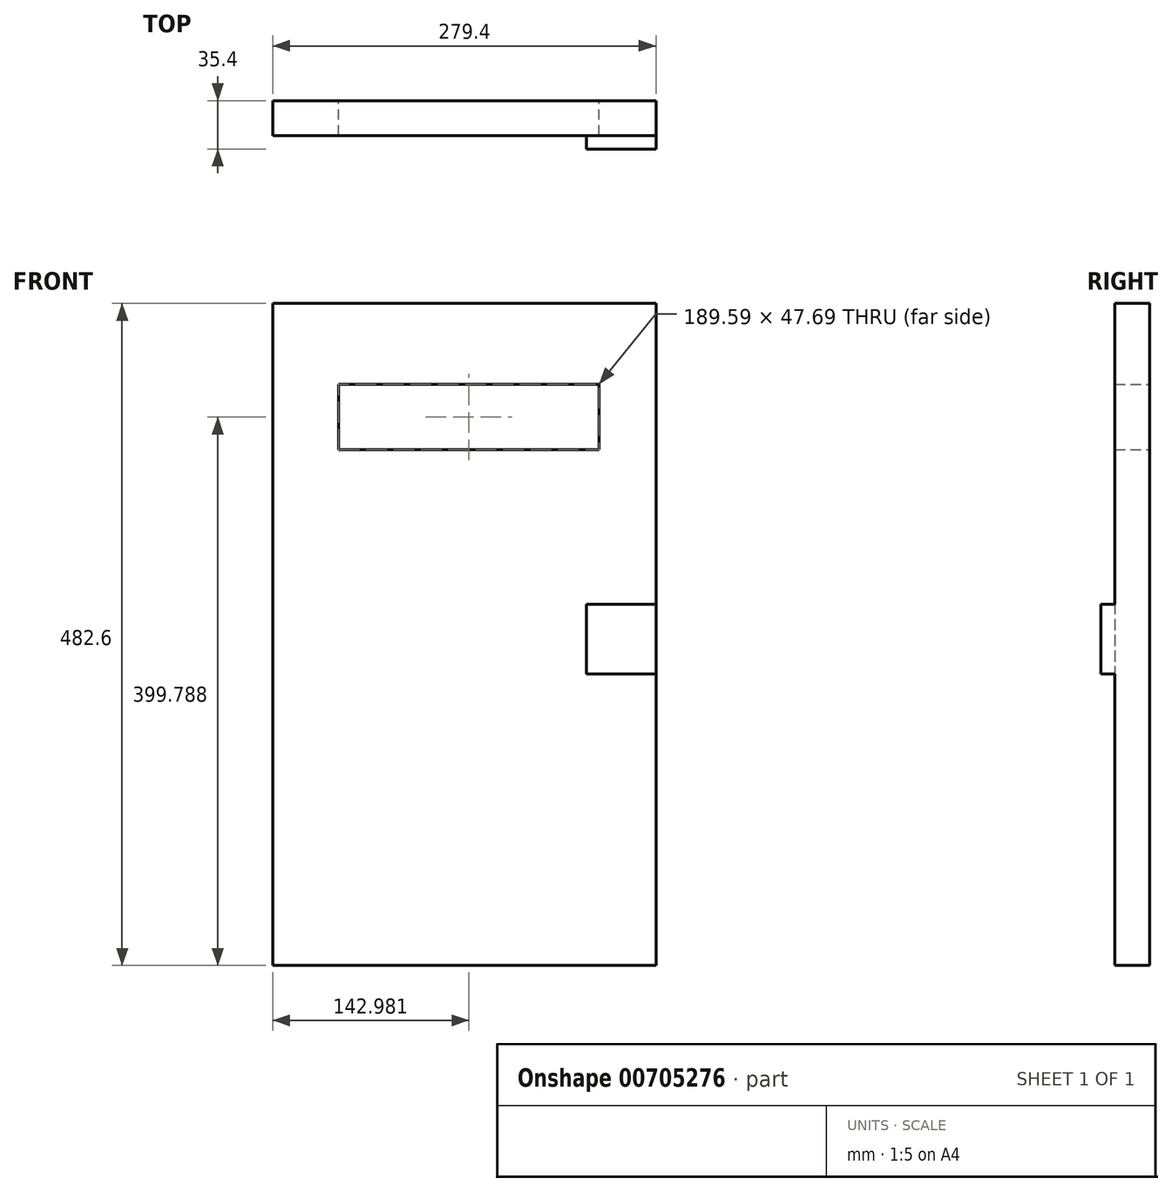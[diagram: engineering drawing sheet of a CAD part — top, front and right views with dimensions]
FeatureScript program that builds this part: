
annotation { "Feature Type Name" : "Feature", "Feature Type Description" : "" }
export const myFeature = defineFeature(function(context is Context, id is Id, definition is map)
    precondition{}
    {
        {
            var Q0;
            Q0=qCreatedBy(makeId("Front.planeOp"),FACE);
            var sketch = newSketch(context, id + "F0", { "sketchPlane" : qUnion([Q0])});
            skLineSegment(sketch, "E0.bottom", {"start": v(139.7, 241.3) * mm, "end": v(-139.7, 241.3) * mm});
            skLineSegment(sketch, "E0.top", {"start": v(139.7, -241.3) * mm, "end": v(-139.7, -241.3) * mm});
            skLineSegment(sketch, "E0.left", {"start": v(139.7, 241.3) * mm, "end": v(139.7, -241.3) * mm});
            skLineSegment(sketch, "E0.right", {"start": v(-139.7, 241.3) * mm, "end": v(-139.7, -241.3) * mm});
            skPoint(sketch, "E0.middle", {"position": v(0, 0) * mm});
            skLineSegment(sketch, "E1", {"start": v(-91.51, 182.33) * mm, "end": v(98.07, 182.33) * mm});
            skLineSegment(sketch, "E2", {"start": v(-91.51, 182.33) * mm, "end": v(-91.51, 134.64) * mm});
            skLineSegment(sketch, "E3", {"start": v(98.07, 182.33) * mm, "end": v(98.07, 134.64) * mm});
            skLineSegment(sketch, "E4", {"start": v(98.07, 134.64) * mm, "end": v(-91.51, 134.64) * mm});
            skLineSegment(sketch, "E5", {"start": v(-91.51, 158.49) * mm, "end": v(98.07, 158.49) * mm});
            skSolve(sketch);
        }
        {
            var Q0;
            Q0=makeQuery(id+"F0.imprint","IMPRINT",FACE,{"disambiguationData":[TD([[makeQuery(id+"F0.imprint","IMPRINT",EDGE,{"derivedFrom":sQuery(id+"F0.wireOp",EDGE,"E0.bottom")}),1.0]])]});
            extrude(context, id + "F1", {"entities" : qUnion([Q0]), "depth" : 25.4 * mm, "offsetDistance" : 25.4 * mm});
        }
        {
            var Q0;
            Q0=makeQuery(id+"F1.opExtrude","CAP_FACE",FACE,{"disambiguationData":[OSD([sQuery(id+"F0.wireOp",EDGE,"E0.bottom"),sQuery(id+"F0.wireOp",EDGE,"E0.top"),sQuery(id+"F0.wireOp",EDGE,"E0.left"),sQuery(id+"F0.wireOp",EDGE,"E0.right"),sQuery(id+"F0.wireOp",EDGE,"E1"),sQuery(id+"F0.wireOp",EDGE,"E2"),sQuery(id+"F0.wireOp",EDGE,"E3"),sQuery(id+"F0.wireOp",EDGE,"E4")])],"isStart":false});
            var sketch = newSketch(context, id + "F2", { "sketchPlane" : qUnion([Q0])});
            skLineSegment(sketch, "E6", {"start": v(139.7, 22.09) * mm, "end": v(88.9, 22.09) * mm});
            skLineSegment(sketch, "E7", {"start": v(88.9, 22.09) * mm, "end": v(88.9, -28.71) * mm});
            skLineSegment(sketch, "E8", {"start": v(88.9, -28.71) * mm, "end": v(139.7, -28.71) * mm});
            skCircle(sketch, "E9", {"center": v(114.3, -3.31) * mm, "radius": 25.4 * mm});
            skPoint(sketch, "E10.orphan", {"position": v(114.3, 22.09) * mm});
            skPoint(sketch, "E11.end.orphan", {"position": v(114.3, -28.71) * mm});
            skSolve(sketch);
        }
        {
            var Q0;
            {var subQ0=sQuery(id+"F2.wireOp",EDGE,"E8");var subQ1=sQuery(id+"F2.wireOp",EDGE,"E7");var subQ2=makeQuery(id+"F2.imprint","INTERSECT",VERTEX,{"derivedFrom":[subQ1,subQ0]});Q0=makeQuery(id+"F2.imprint","IMPRINT",FACE,{"disambiguationData":[TD([[makeQuery(id+"F2.imprint","IMPRINT",EDGE,{"disambiguationData":[TD([[subQ2,1.0]])],"derivedFrom":subQ1}),1.0]])]});}
            var Q1;
            {var subQ0=sQuery(id+"F2.wireOp",EDGE,"E8");var subQ1=makeQuery(id+"F1.opExtrude","CAP_EDGE",EDGE,{"disambiguationData":[OSD([sQuery(id+"F0.wireOp",EDGE,"E0.left")])],"isStart":false});var subQ2=makeQuery(id+"F2.imprint","INTERSECT",VERTEX,{"derivedFrom":[subQ1,subQ0]});Q1=makeQuery(id+"F2.imprint","IMPRINT",FACE,{"disambiguationData":[TD([[makeQuery(id+"F2.imprint","IMPRINT",EDGE,{"disambiguationData":[TD([[subQ2,1.0]])],"derivedFrom":subQ0}),1.0]])]});}
            var Q2;
            {var subQ0=sQuery(id+"F2.wireOp",EDGE,"E7");var subQ1=sQuery(id+"F2.wireOp",EDGE,"E6");var subQ2=makeQuery(id+"F2.imprint","INTERSECT",VERTEX,{"derivedFrom":[subQ1,subQ0]});Q2=makeQuery(id+"F2.imprint","IMPRINT",FACE,{"disambiguationData":[TD([[makeQuery(id+"F2.imprint","IMPRINT",EDGE,{"disambiguationData":[TD([[subQ2,1.0]])],"derivedFrom":subQ1}),1.0]])]});}
            var Q3;
            {var subQ0=sQuery(id+"F2.wireOp",EDGE,"E9");var subQ1=makeQuery(id+"F2.imprint","INTERSECT",VERTEX,{"derivedFrom":[sQuery(id+"F2.wireOp",EDGE,"E6"),subQ0]});Q3=makeQuery(id+"F2.imprint","IMPRINT",FACE,{"disambiguationData":[TD([[makeQuery(id+"F2.imprint","IMPRINT",EDGE,{"disambiguationData":[TD([[subQ1,1.0]])],"derivedFrom":subQ0}),1.0]])]});}
            var Q4;
            {var subQ0=sQuery(id+"F2.wireOp",EDGE,"E6");var subQ1=makeQuery(id+"F1.opExtrude","CAP_EDGE",EDGE,{"disambiguationData":[OSD([sQuery(id+"F0.wireOp",EDGE,"E0.left")])],"isStart":false});var subQ2=makeQuery(id+"F2.imprint","INTERSECT",VERTEX,{"derivedFrom":[subQ1,subQ0]});Q4=makeQuery(id+"F2.imprint","IMPRINT",FACE,{"disambiguationData":[TD([[makeQuery(id+"F2.imprint","IMPRINT",EDGE,{"disambiguationData":[TD([[subQ2,-1.0]])],"derivedFrom":subQ0}),1.0]])]});}
            extrude(context, id + "F3", {"entities" : qUnion([Q0, Q1, Q2, Q3, Q4]), "operationType" : NewBodyOperationType.ADD, "depth" : 10 * mm, "offsetDistance" : 25.4 * mm});
        }
    });
